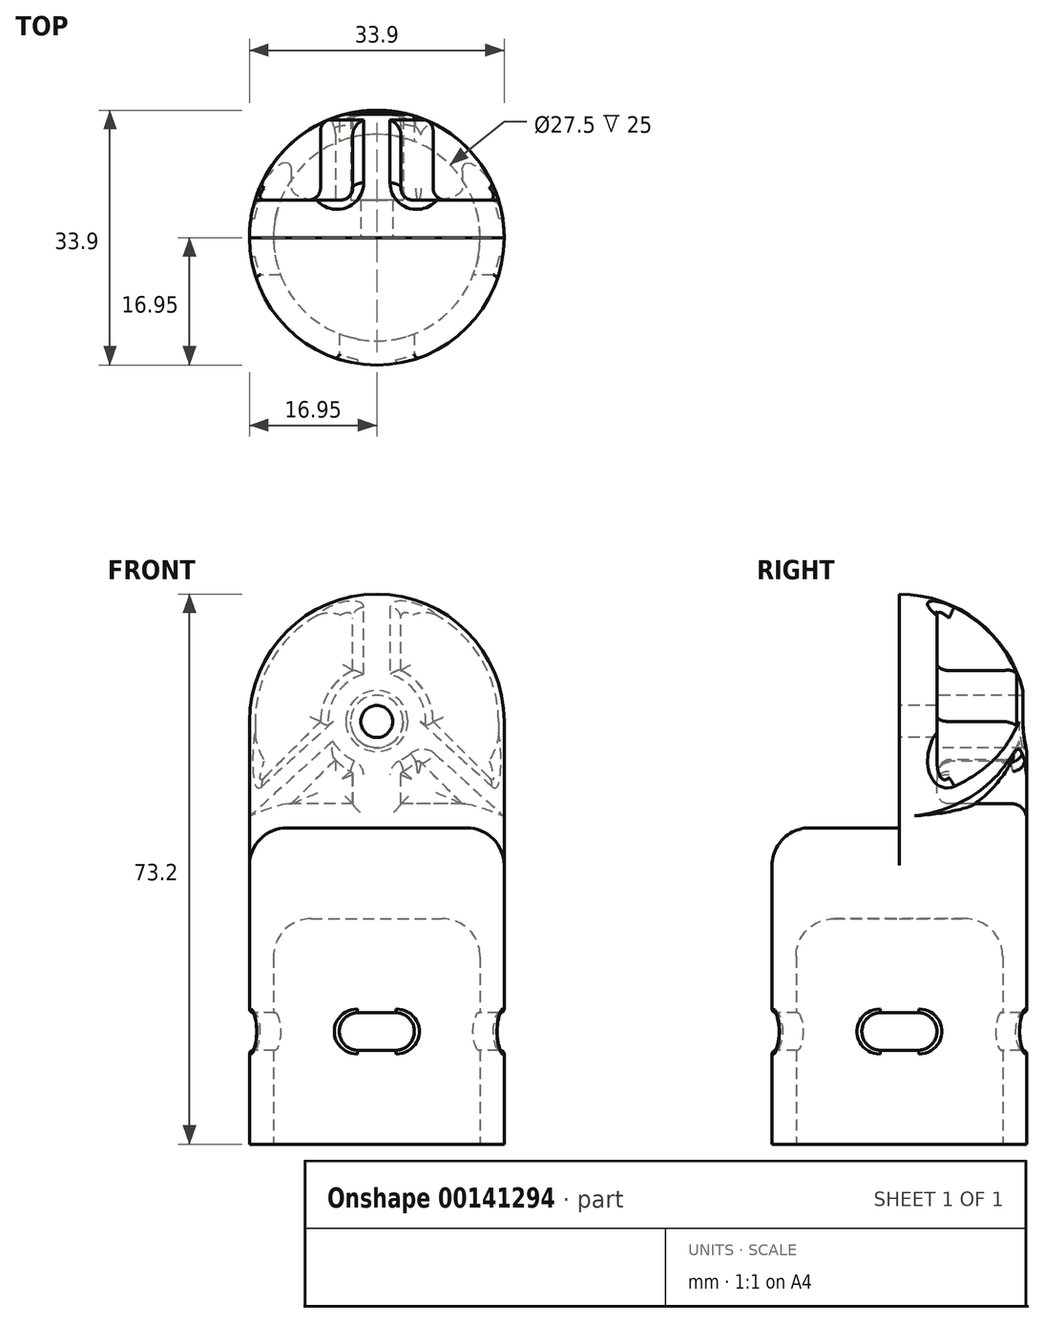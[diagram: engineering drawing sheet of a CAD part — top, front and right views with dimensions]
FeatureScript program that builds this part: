
annotation { "Feature Type Name" : "Feature", "Feature Type Description" : "" }
export const myFeature = defineFeature(function(context is Context, id is Id, definition is map)
    precondition{}
    {
        {
            var Q0;
            Q0=qCreatedBy(makeId("Front.planeOp"),FACE);
            var sketch = newSketch(context, id + "F0", { "sketchPlane" : qUnion([Q0])});
            skLineSegment(sketch, "E0", {"start": v(13.75, 0) * mm, "end": v(13.75, 25) * mm});
            skLineSegment(sketch, "E1", {"start": v(8.75, 30) * mm, "end": v(0, 30) * mm});
            skLineSegment(sketch, "E2", {"start": v(0, 30) * mm, "end": v(0, 33.2) * mm});
            skLineSegment(sketch, "E3", {"start": v(0, 33.2) * mm, "end": v(16.95, 33.2) * mm, "construction": true});
            skLineSegment(sketch, "E4", {"start": v(16.95, 33.2) * mm, "end": v(16.95, 0) * mm});
            skLineSegment(sketch, "E5", {"start": v(16.95, 0) * mm, "end": v(13.75, 0) * mm});
            skPoint(sketch, "E6.visualSharp", {"position": v(13.75, 30) * mm});
            skArc(sketch, "E6.filletArc", {"start": v(13.75, 25) * mm, "mid": v(12.29, 28.54) * mm, "end": v(8.75, 30) * mm});
            skLineSegment(sketch, "E7", {"start": v(16.95, 33.2) * mm, "end": v(16.95, 56.25) * mm});
            skLineSegment(sketch, "E8", {"start": v(0, 73.2) * mm, "end": v(0, 73.2) * mm});
            skLineSegment(sketch, "E9", {"start": v(0, 73.2) * mm, "end": v(0, 33.2) * mm});
            skPoint(sketch, "E10.visualSharp", {"position": v(16.95, 73.2) * mm});
            skArc(sketch, "E10.filletArc", {"start": v(16.95, 56.25) * mm, "mid": v(11.99, 68.24) * mm, "end": v(0, 73.2) * mm});
            skSolve(sketch);
        }
        {
            var Q0;
            Q0=qSketchRegion(id+"F0",true);
            var Q1;
            Q1=sQuery(id+"F0.wireOp",EDGE,"E2");
            revolve(context, id + "F1", {"entities" : qUnion([Q0]), "axis" : qUnion([Q1]), "revolveType" : RevolveType.FULL});
        }
        {
            var Q0;
            Q0=qCreatedBy(makeId("Front.planeOp"),FACE);
            var sketch = newSketch(context, id + "F2", { "sketchPlane" : qUnion([Q0])});
            skArc(sketch, "E11", {"start": v(20.45, 56.25) * mm, "mid": v(0, 76.7) * mm, "end": v(-20.45, 56.25) * mm});
            skLineSegment(sketch, "E12", {"start": v(-20.45, 56.25) * mm, "end": v(-20.45, 42.1) * mm});
            skLineSegment(sketch, "E13", {"start": v(-20.45, 42.1) * mm, "end": v(20.45, 42.1) * mm});
            skLineSegment(sketch, "E14", {"start": v(20.45, 42.1) * mm, "end": v(20.45, 56.25) * mm});
            skSolve(sketch);
        }
        {
            var Q0;
            Q0=qSketchRegion(id+"F2",true);
            extrude(context, id + "F3", {"entities" : qUnion([Q0]), "operationType" : NewBodyOperationType.REMOVE, "depth" : 25 * mm});
        }
        {
            var Q0;
            Q0=qCreatedBy(makeId("Front.planeOp"),FACE);
            cPlane(context, id + "F4", {"entities" : qUnion([Q0]), "cplaneType" : CPlaneType.OFFSET, "offset" : 5 * mm, "oppositeDirection" : true, "width" : 150 * mm, "height" : 150 * mm});
        }
        {
            var Q0;
            Q0=makeQuery(id+"F3.boolean.opBoolean","INTERSECT",EDGE,{"derivedFrom":[makeQuery(id+"F1.opRevolve","SWEPT_FACE",FACE,{"disambiguationData":[OSD([sQuery(id+"F0.wireOp",EDGE,"E4"),sQuery(id+"F0.wireOp",EDGE,"E7")])]}),makeQuery(id+"F3.opExtrude","SWEPT_FACE",FACE,{"disambiguationData":[OSD([sQuery(id+"F2.wireOp",EDGE,"E13")])]})]});
            fillet(context, id + "F5", {"entities" : qUnion([Q0]), "radius" : 5 * mm, "tangentPropagation" : true, "allowEdgeOverflow" : false});
        }
        {
            var Q0;
            Q0=qCreatedBy(makeId("Front.planeOp"),FACE);
            var sketch = newSketch(context, id + "F6", { "sketchPlane" : qUnion([Q0])});
            skLineSegment(sketch, "E15.bottom", {"start": v(2.5, 12.5) * mm, "end": v(-2.5, 12.5) * mm});
            skLineSegment(sketch, "E15.top", {"start": v(2.5, 17.5) * mm, "end": v(-2.5, 17.5) * mm});
            skLineSegment(sketch, "E15.left", {"start": v(5, 15) * mm, "end": v(5, 15) * mm});
            skLineSegment(sketch, "E15.right", {"start": v(-5, 15) * mm, "end": v(-5, 15) * mm});
            skPoint(sketch, "E15.middle", {"position": v(0, 15) * mm});
            skPoint(sketch, "E16.visualSharp", {"position": v(-5, 17.5) * mm});
            skArc(sketch, "E16.filletArc", {"start": v(-2.5, 17.5) * mm, "mid": v(-4.27, 16.77) * mm, "end": v(-5, 15) * mm});
            skPoint(sketch, "E17.visualSharp", {"position": v(-5, 12.5) * mm});
            skArc(sketch, "E17.filletArc", {"start": v(-5, 15) * mm, "mid": v(-4.27, 13.23) * mm, "end": v(-2.5, 12.5) * mm});
            skPoint(sketch, "E18.visualSharp", {"position": v(5, 12.5) * mm});
            skArc(sketch, "E18.filletArc", {"start": v(2.5, 12.5) * mm, "mid": v(4.27, 13.23) * mm, "end": v(5, 15) * mm});
            skPoint(sketch, "E19.visualSharp", {"position": v(5, 17.5) * mm});
            skArc(sketch, "E19.filletArc", {"start": v(5, 15) * mm, "mid": v(4.27, 16.77) * mm, "end": v(2.5, 17.5) * mm});
            skSolve(sketch);
        }
        {
            var Q0;
            Q0=qSketchRegion(id+"F6",true);
            extrude(context, id + "F7", {"entities" : qUnion([Q0]), "operationType" : NewBodyOperationType.REMOVE, "endBound" : BoundingType.SYMMETRIC, "oppositeDirection" : true, "depth" : 60 * mm});
        }
        {
            var Q0;
            Q0=qCreatedBy(makeId("Right.planeOp"),FACE);
            var sketch = newSketch(context, id + "F8", { "sketchPlane" : qUnion([Q0])});
            skLineSegment(sketch, "E20.bottom", {"start": v(2.5, 12.5) * mm, "end": v(-2.5, 12.5) * mm});
            skLineSegment(sketch, "E20.top", {"start": v(2.5, 17.5) * mm, "end": v(-2.5, 17.5) * mm});
            skLineSegment(sketch, "E20.left", {"start": v(5, 15) * mm, "end": v(5, 15) * mm});
            skLineSegment(sketch, "E20.right", {"start": v(-5, 15) * mm, "end": v(-5, 15) * mm});
            skPoint(sketch, "E20.middle", {"position": v(0, 15) * mm});
            skPoint(sketch, "E21.visualSharp", {"position": v(-5, 17.5) * mm});
            skArc(sketch, "E21.filletArc", {"start": v(-2.5, 17.5) * mm, "mid": v(-4.27, 16.77) * mm, "end": v(-5, 15) * mm});
            skPoint(sketch, "E22.visualSharp", {"position": v(5, 17.5) * mm});
            skArc(sketch, "E22.filletArc", {"start": v(5, 15) * mm, "mid": v(4.27, 16.77) * mm, "end": v(2.5, 17.5) * mm});
            skPoint(sketch, "E23.visualSharp", {"position": v(5, 12.5) * mm});
            skArc(sketch, "E23.filletArc", {"start": v(2.5, 12.5) * mm, "mid": v(4.27, 13.23) * mm, "end": v(5, 15) * mm});
            skPoint(sketch, "E24.visualSharp", {"position": v(-5, 12.5) * mm});
            skArc(sketch, "E24.filletArc", {"start": v(-5, 15) * mm, "mid": v(-4.27, 13.23) * mm, "end": v(-2.5, 12.5) * mm});
            skSolve(sketch);
        }
        {
            var Q0;
            Q0=qSketchRegion(id+"F8",true);
            extrude(context, id + "F9", {"entities" : qUnion([Q0]), "operationType" : NewBodyOperationType.REMOVE, "endBound" : BoundingType.SYMMETRIC, "depth" : 60 * mm});
        }
        {
            var Q0;
            Q0=qCreatedBy(id+"F4.planeOp",FACE);
            var sketch = newSketch(context, id + "F10", { "sketchPlane" : qUnion([Q0])});
            skArc(sketch, "E25", {"start": v(-16.95, 56.25) * mm, "mid": v(-13.07, 67.04) * mm, "end": v(-3.2, 72.9) * mm});
            skLineSegment(sketch, "E26", {"start": v(16.95, 56.25) * mm, "end": v(16.95, 46.8) * mm});
            skLineSegment(sketch, "E27", {"start": v(11.38, 45.3) * mm, "end": v(3.2, 45.3) * mm});
            skLineSegment(sketch, "E28", {"start": v(-16.95, 46.8) * mm, "end": v(-16.95, 56.25) * mm});
            skArc(sketch, "E29", {"start": v(7.5, 56.25) * mm, "mid": v(6.33, 60.27) * mm, "end": v(3.2, 63.03) * mm});
            skLineSegment(sketch, "E30.left", {"start": v(3.2, 45.3) * mm, "end": v(3.2, 49.47) * mm});
            skLineSegment(sketch, "E30.right", {"start": v(-3.2, 45.3) * mm, "end": v(-3.2, 49.47) * mm});
            skLineSegment(sketch, "E31", {"start": v(-16.95, 46.8) * mm, "end": v(-7.5, 56.25) * mm});
            skLineSegment(sketch, "E32", {"start": v(16.95, 46.8) * mm, "end": v(7.5, 56.25) * mm});
            skLineSegment(sketch, "E33", {"start": v(3.2, 63.03) * mm, "end": v(3.2, 72.9) * mm});
            skLineSegment(sketch, "E34", {"start": v(-3.2, 63.03) * mm, "end": v(-3.2, 72.9) * mm});
            skArc(sketch, "E35.trimOffspring", {"start": v(-3.2, 63.03) * mm, "mid": v(-6.33, 60.27) * mm, "end": v(-7.5, 56.25) * mm});
            skArc(sketch, "E36.trimOffspring", {"start": v(3.2, 72.9) * mm, "mid": v(13.07, 67.04) * mm, "end": v(16.95, 56.25) * mm});
            skLineSegment(sketch, "E37", {"start": v(11.38, 45.3) * mm, "end": v(5.51, 51.17) * mm});
            skLineSegment(sketch, "E38", {"start": v(-11.38, 45.3) * mm, "end": v(-5.51, 51.17) * mm});
            skArc(sketch, "E39", {"start": v(3.2, 49.47) * mm, "mid": v(4.44, 50.2) * mm, "end": v(5.51, 51.17) * mm});
            skArc(sketch, "E40", {"start": v(-3.2, 49.47) * mm, "mid": v(-4.44, 50.2) * mm, "end": v(-5.51, 51.17) * mm});
            skCircle(sketch, "E41", {"center": v(0, 56.25) * mm, "radius": 3.5 * mm});
            skLineSegment(sketch, "E42.trimOffspring", {"start": v(-3.2, 45.3) * mm, "end": v(-11.38, 45.3) * mm});
            skSolve(sketch);
        }
        {
            var Q0;
            Q0 = qSketchRegion(id + "F10", true);
            extrude(context, id + "F11", {"entities" : qUnion([Q0]), "operationType" : NewBodyOperationType.REMOVE, "endBound" : BoundingType.THROUGH_ALL, "oppositeDirection" : true, "depth" : 25 * mm});
        }
        {
            var Q0;
            Q0=makeQuery(id+"F3.boolean.opBoolean","COPY",FACE,{"derivedFrom":makeQuery(id+"F3.opExtrude","CAP_FACE",FACE,{"disambiguationData":[OSD([sQuery(id+"F2.wireOp",EDGE,"E11"),sQuery(id+"F2.wireOp",EDGE,"E12"),sQuery(id+"F2.wireOp",EDGE,"E13"),sQuery(id+"F2.wireOp",EDGE,"E14")])],"isStart":true})});
            var sketch = newSketch(context, id + "F12", { "sketchPlane" : qUnion([Q0])});
            skCircle(sketch, "E43", {"center": v(0, 56.25) * mm, "radius": 2.12 * mm});
            skSolve(sketch);
        }
        {
            var Q0;
            Q0=qSketchRegion(id+"F12",true);
            extrude(context, id + "F13", {"entities" : qUnion([Q0]), "operationType" : NewBodyOperationType.REMOVE, "endBound" : BoundingType.THROUGH_ALL, "oppositeDirection" : true, "depth" : 25 * mm});
        }
        {
            var Q0;
            Q0=makeQuery(id+"F11.boolean.opBoolean","INTERSECT",EDGE,{"derivedFrom":[makeQuery(id+"F1.opRevolve","SWEPT_FACE",FACE,{"disambiguationData":[OSD([sQuery(id+"F0.wireOp",EDGE,"E10.filletArc")])]}),makeQuery(id+"F11.opExtrude","SWEPT_FACE",FACE,{"disambiguationData":[OSD([sQuery(id+"F10.wireOp",EDGE,"E41")])]})]});
            var Q1;
            Q1=makeQuery(id+"F11.boolean.opBoolean","INTERSECT",EDGE,{"derivedFrom":[makeQuery(id+"F1.opRevolve","SWEPT_FACE",FACE,{"disambiguationData":[OSD([sQuery(id+"F0.wireOp",EDGE,"E4"),sQuery(id+"F0.wireOp",EDGE,"E7")])]}),makeQuery(id+"F11.opExtrude","SWEPT_FACE",FACE,{"disambiguationData":[OSD([sQuery(id+"F10.wireOp",EDGE,"E41")])]})]});
            var Q2;
            Q2=makeQuery(id+"F7.boolean.opBoolean","INTERSECT",EDGE,{"disambiguationData":[OD(1.0)],"derivedFrom":[makeQuery(id+"F1.opRevolve","SWEPT_FACE",FACE,{"disambiguationData":[OSD([sQuery(id+"F0.wireOp",EDGE,"E4"),sQuery(id+"F0.wireOp",EDGE,"E7")])]}),makeQuery(id+"F7.opExtrude","SWEPT_FACE",FACE,{"disambiguationData":[OSD([sQuery(id+"F6.wireOp",EDGE,"E16.filletArc"),sQuery(id+"F6.wireOp",EDGE,"E17.filletArc")])]})]});
            var Q3;
            Q3=makeQuery(id+"F9.boolean.opBoolean","INTERSECT",EDGE,{"disambiguationData":[OD(1.0)],"derivedFrom":[makeQuery(id+"F1.opRevolve","SWEPT_FACE",FACE,{"disambiguationData":[OSD([sQuery(id+"F0.wireOp",EDGE,"E4"),sQuery(id+"F0.wireOp",EDGE,"E7")])]}),makeQuery(id+"F9.opExtrude","SWEPT_FACE",FACE,{"disambiguationData":[OSD([sQuery(id+"F8.wireOp",EDGE,"E22.filletArc"),sQuery(id+"F8.wireOp",EDGE,"E23.filletArc")])]})]});
            var Q4;
            Q4=makeQuery(id+"F7.boolean.opBoolean","INTERSECT",EDGE,{"disambiguationData":[OD(0.0)],"derivedFrom":[makeQuery(id+"F1.opRevolve","SWEPT_FACE",FACE,{"disambiguationData":[OSD([sQuery(id+"F0.wireOp",EDGE,"E4"),sQuery(id+"F0.wireOp",EDGE,"E7")])]}),makeQuery(id+"F7.opExtrude","SWEPT_FACE",FACE,{"disambiguationData":[OSD([sQuery(id+"F6.wireOp",EDGE,"E18.filletArc"),sQuery(id+"F6.wireOp",EDGE,"E19.filletArc")])]})]});
            var Q5;
            Q5=makeQuery(id+"F9.boolean.opBoolean","INTERSECT",EDGE,{"disambiguationData":[OD(0.0)],"derivedFrom":[makeQuery(id+"F1.opRevolve","SWEPT_FACE",FACE,{"disambiguationData":[OSD([sQuery(id+"F0.wireOp",EDGE,"E4"),sQuery(id+"F0.wireOp",EDGE,"E7")])]}),makeQuery(id+"F9.opExtrude","SWEPT_FACE",FACE,{"disambiguationData":[OSD([sQuery(id+"F8.wireOp",EDGE,"E21.filletArc"),sQuery(id+"F8.wireOp",EDGE,"E24.filletArc")])]})]});
            var Q6;
            Q6=makeQuery(id+"F11.boolean.opBoolean","COPY",EDGE,{"derivedFrom":makeQuery(id+"F11.opExtrude","SWEPT_EDGE",EDGE,{"disambiguationData":[OSD([sQuery(id+"F10.wireOp",EDGE,"E30.left"),sQuery(id+"F10.wireOp",EDGE,"E39")])]})});
            var Q7;
            Q7=makeQuery(id+"F11.boolean.opBoolean","COPY",EDGE,{"derivedFrom":makeQuery(id+"F11.opExtrude","SWEPT_EDGE",EDGE,{"disambiguationData":[OSD([sQuery(id+"F10.wireOp",EDGE,"E37"),sQuery(id+"F10.wireOp",EDGE,"E39")])]})});
            var Q8;
            Q8=makeQuery(id+"F11.boolean.opBoolean","COPY",EDGE,{"derivedFrom":makeQuery(id+"F11.opExtrude","SWEPT_EDGE",EDGE,{"disambiguationData":[OSD([sQuery(id+"F10.wireOp",EDGE,"E30.right"),sQuery(id+"F10.wireOp",EDGE,"E40")])]})});
            fillet(context, id + "F14", {"entities" : qUnion([Q0, Q1, Q2, Q3, Q4, Q5, Q6, Q7, Q8]), "radius" : .5 * mm, "tangentPropagation" : true, "allowEdgeOverflow" : false});
        }
        {
            var Q0;
            Q0=makeQuery(id+"F11.boolean.opBoolean","INTERSECT",EDGE,{"derivedFrom":[makeQuery(id+"F1.opRevolve","SWEPT_FACE",FACE,{"disambiguationData":[OSD([sQuery(id+"F0.wireOp",EDGE,"E10.filletArc")])]}),makeQuery(id+"F11.opExtrude","SWEPT_FACE",FACE,{"disambiguationData":[OSD([sQuery(id+"F10.wireOp",EDGE,"E33")])]})]});
            var Q1;
            Q1=makeQuery(id+"F11.boolean.opBoolean","INTERSECT",EDGE,{"derivedFrom":[makeQuery(id+"F1.opRevolve","SWEPT_FACE",FACE,{"disambiguationData":[OSD([sQuery(id+"F0.wireOp",EDGE,"E10.filletArc")])]}),makeQuery(id+"F11.opExtrude","SWEPT_FACE",FACE,{"disambiguationData":[OSD([sQuery(id+"F10.wireOp",EDGE,"E34")])]})]});
            var Q2;
            Q2=makeQuery(id+"F11.boolean.opBoolean","INTERSECT",EDGE,{"derivedFrom":[makeQuery(id+"F1.opRevolve","SWEPT_FACE",FACE,{"disambiguationData":[OSD([sQuery(id+"F0.wireOp",EDGE,"E10.filletArc")])]}),makeQuery(id+"F11.opExtrude","SWEPT_FACE",FACE,{"disambiguationData":[OSD([sQuery(id+"F10.wireOp",EDGE,"E35.trimOffspring")])]})]});
            var Q3;
            Q3=makeQuery(id+"F11.boolean.opBoolean","INTERSECT",EDGE,{"derivedFrom":[makeQuery(id+"F1.opRevolve","SWEPT_FACE",FACE,{"disambiguationData":[OSD([sQuery(id+"F0.wireOp",EDGE,"E10.filletArc")])]}),makeQuery(id+"F11.opExtrude","SWEPT_FACE",FACE,{"disambiguationData":[OSD([sQuery(id+"F10.wireOp",EDGE,"E29")])]})]});
            var Q4;
            Q4=makeQuery(id+"F11.boolean.opBoolean","INTERSECT",EDGE,{"derivedFrom":[makeQuery(id+"F1.opRevolve","SWEPT_FACE",FACE,{"disambiguationData":[OSD([sQuery(id+"F0.wireOp",EDGE,"E4"),sQuery(id+"F0.wireOp",EDGE,"E7")])]}),makeQuery(id+"F11.opExtrude","SWEPT_FACE",FACE,{"disambiguationData":[OSD([sQuery(id+"F10.wireOp",EDGE,"E32")])]})]});
            var Q5;
            Q5=makeQuery(id+"F11.boolean.opBoolean","INTERSECT",EDGE,{"derivedFrom":[makeQuery(id+"F1.opRevolve","SWEPT_FACE",FACE,{"disambiguationData":[OSD([sQuery(id+"F0.wireOp",EDGE,"E4"),sQuery(id+"F0.wireOp",EDGE,"E7")])]}),makeQuery(id+"F11.opExtrude","SWEPT_FACE",FACE,{"disambiguationData":[OSD([sQuery(id+"F10.wireOp",EDGE,"E31")])]})]});
            var Q6;
            Q6=makeQuery(id+"F11.boolean.opBoolean","INTERSECT",EDGE,{"derivedFrom":[makeQuery(id+"F1.opRevolve","SWEPT_FACE",FACE,{"disambiguationData":[OSD([sQuery(id+"F0.wireOp",EDGE,"E4"),sQuery(id+"F0.wireOp",EDGE,"E7")])]}),makeQuery(id+"F11.opExtrude","SWEPT_FACE",FACE,{"disambiguationData":[OSD([sQuery(id+"F10.wireOp",EDGE,"E38")])]})]});
            var Q7;
            Q7=makeQuery(id+"F11.boolean.opBoolean","INTERSECT",EDGE,{"derivedFrom":[makeQuery(id+"F1.opRevolve","SWEPT_FACE",FACE,{"disambiguationData":[OSD([sQuery(id+"F0.wireOp",EDGE,"E4"),sQuery(id+"F0.wireOp",EDGE,"E7")])]}),makeQuery(id+"F11.opExtrude","SWEPT_FACE",FACE,{"disambiguationData":[OSD([sQuery(id+"F10.wireOp",EDGE,"E42.trimOffspring")])]})]});
            var Q8;
            Q8=makeQuery(id+"F11.boolean.opBoolean","INTERSECT",EDGE,{"derivedFrom":[makeQuery(id+"F1.opRevolve","SWEPT_FACE",FACE,{"disambiguationData":[OSD([sQuery(id+"F0.wireOp",EDGE,"E4"),sQuery(id+"F0.wireOp",EDGE,"E7")])]}),makeQuery(id+"F11.opExtrude","SWEPT_FACE",FACE,{"disambiguationData":[OSD([sQuery(id+"F10.wireOp",EDGE,"E30.right")])]})]});
            var Q9;
            Q9=makeQuery(id+"F11.boolean.opBoolean","INTERSECT",EDGE,{"derivedFrom":[makeQuery(id+"F1.opRevolve","SWEPT_FACE",FACE,{"disambiguationData":[OSD([sQuery(id+"F0.wireOp",EDGE,"E4"),sQuery(id+"F0.wireOp",EDGE,"E7")])]}),makeQuery(id+"F11.opExtrude","SWEPT_FACE",FACE,{"disambiguationData":[OSD([sQuery(id+"F10.wireOp",EDGE,"E30.left")])]})]});
            var Q10;
            Q10=makeQuery(id+"F11.boolean.opBoolean","INTERSECT",EDGE,{"derivedFrom":[makeQuery(id+"F1.opRevolve","SWEPT_FACE",FACE,{"disambiguationData":[OSD([sQuery(id+"F0.wireOp",EDGE,"E4"),sQuery(id+"F0.wireOp",EDGE,"E7")])]}),makeQuery(id+"F11.opExtrude","SWEPT_FACE",FACE,{"disambiguationData":[OSD([sQuery(id+"F10.wireOp",EDGE,"E27")])]})]});
            var Q11;
            Q11=makeQuery(id+"F11.boolean.opBoolean","COPY",EDGE,{"derivedFrom":makeQuery(id+"F11.opExtrude","CAP_EDGE",EDGE,{"disambiguationData":[OSD([sQuery(id+"F10.wireOp",EDGE,"E34")])],"isStart":true})});
            var Q12;
            Q12=makeQuery(id+"F11.boolean.opBoolean","COPY",EDGE,{"derivedFrom":makeQuery(id+"F11.opExtrude","CAP_EDGE",EDGE,{"disambiguationData":[OSD([sQuery(id+"F10.wireOp",EDGE,"E35.trimOffspring")])],"isStart":true})});
            var Q13;
            Q13=makeQuery(id+"F11.boolean.opBoolean","COPY",EDGE,{"derivedFrom":makeQuery(id+"F11.opExtrude","CAP_EDGE",EDGE,{"disambiguationData":[OSD([sQuery(id+"F10.wireOp",EDGE,"E31")])],"isStart":true})});
            var Q14;
            Q14=makeQuery(id+"F11.boolean.opBoolean","COPY",EDGE,{"derivedFrom":makeQuery(id+"F11.opExtrude","CAP_EDGE",EDGE,{"disambiguationData":[OSD([sQuery(id+"F10.wireOp",EDGE,"E38")])],"isStart":true})});
            var Q15;
            Q15=makeQuery(id+"F11.boolean.opBoolean","COPY",EDGE,{"derivedFrom":makeQuery(id+"F11.opExtrude","CAP_EDGE",EDGE,{"disambiguationData":[OSD([sQuery(id+"F10.wireOp",EDGE,"E42.trimOffspring")])],"isStart":true})});
            var Q16;
            Q16=makeQuery(id+"F11.boolean.opBoolean","COPY",EDGE,{"derivedFrom":makeQuery(id+"F11.opExtrude","CAP_EDGE",EDGE,{"disambiguationData":[OSD([sQuery(id+"F10.wireOp",EDGE,"E30.right")])],"isStart":true})});
            var Q17;
            Q17=makeQuery(id+"F11.boolean.opBoolean","COPY",EDGE,{"derivedFrom":makeQuery(id+"F11.opExtrude","CAP_EDGE",EDGE,{"disambiguationData":[OSD([sQuery(id+"F10.wireOp",EDGE,"E30.left")])],"isStart":true})});
            var Q18;
            Q18=makeQuery(id+"F11.boolean.opBoolean","COPY",EDGE,{"derivedFrom":makeQuery(id+"F11.opExtrude","CAP_EDGE",EDGE,{"disambiguationData":[OSD([sQuery(id+"F10.wireOp",EDGE,"E27")])],"isStart":true})});
            var Q19;
            Q19=makeQuery(id+"F11.boolean.opBoolean","COPY",EDGE,{"derivedFrom":makeQuery(id+"F11.opExtrude","CAP_EDGE",EDGE,{"disambiguationData":[OSD([sQuery(id+"F10.wireOp",EDGE,"E33")])],"isStart":true})});
            var Q20;
            Q20=makeQuery(id+"F11.boolean.opBoolean","COPY",EDGE,{"derivedFrom":makeQuery(id+"F11.opExtrude","CAP_EDGE",EDGE,{"disambiguationData":[OSD([sQuery(id+"F10.wireOp",EDGE,"E29")])],"isStart":true})});
            var Q21;
            Q21=makeQuery(id+"F11.boolean.opBoolean","COPY",EDGE,{"derivedFrom":makeQuery(id+"F11.opExtrude","CAP_EDGE",EDGE,{"disambiguationData":[OSD([sQuery(id+"F10.wireOp",EDGE,"E32")])],"isStart":true})});
            fillet(context, id + "F15", {"entities" : qUnion([Q0, Q1, Q2, Q3, Q4, Q5, Q6, Q7, Q8, Q9, Q10, Q11, Q12, Q13, Q14, Q15, Q16, Q17, Q18, Q19, Q20, Q21]), "radius" : 1.6 * mm, "tangentPropagation" : true, "allowEdgeOverflow" : false});
        }
    });
